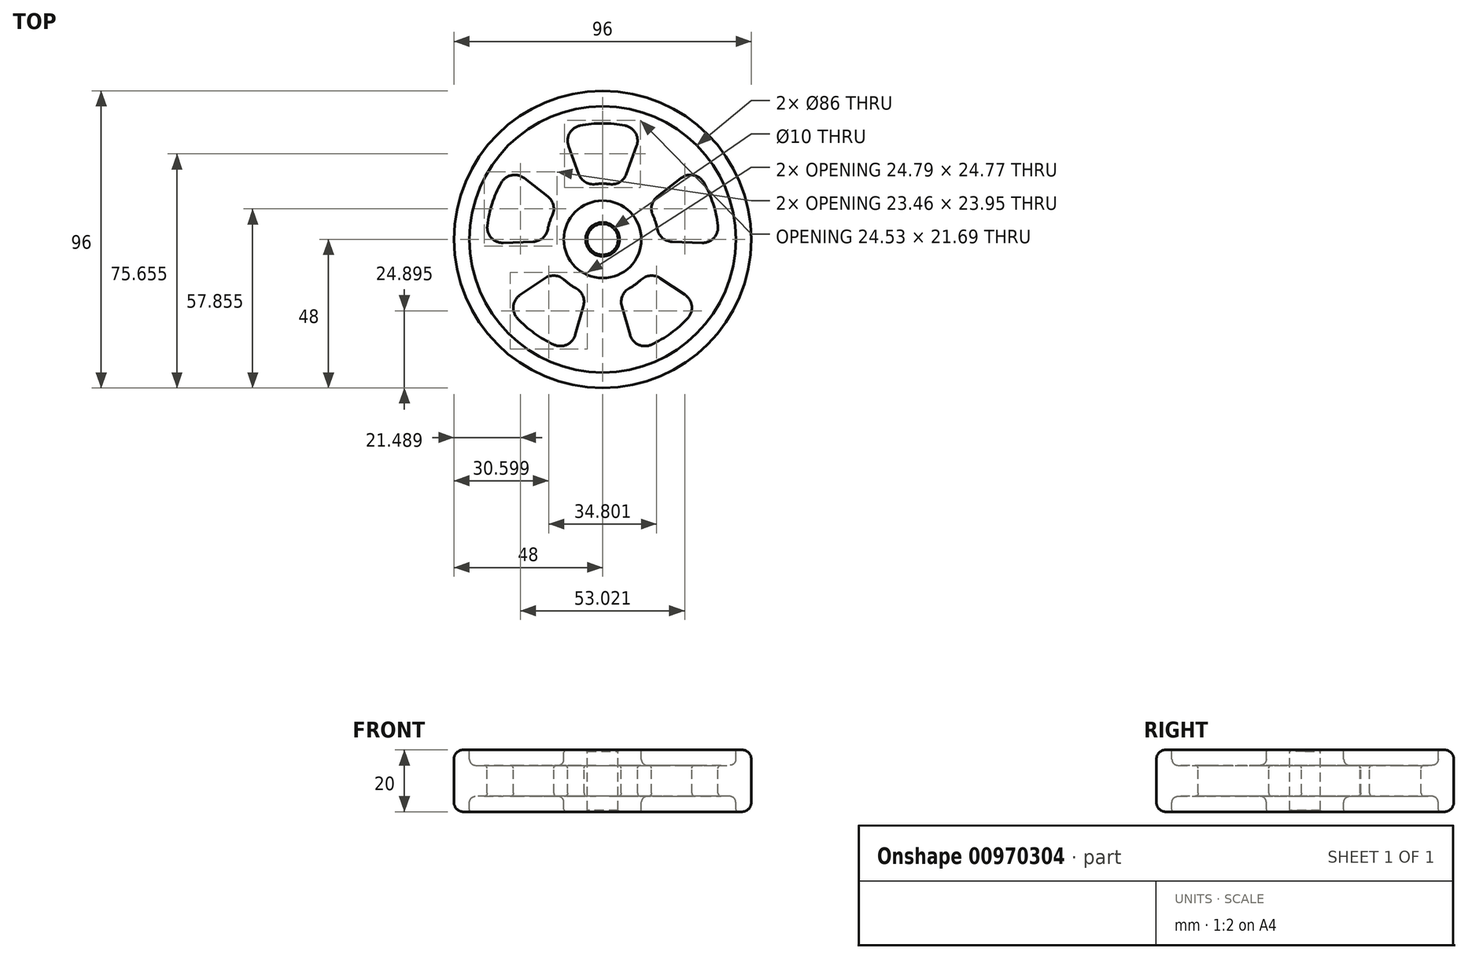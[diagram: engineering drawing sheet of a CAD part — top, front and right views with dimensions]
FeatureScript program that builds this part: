
annotation { "Feature Type Name" : "Feature", "Feature Type Description" : "" }
export const myFeature = defineFeature(function(context is Context, id is Id, definition is map)
    precondition{}
    {
        {
            var Q0;
            Q0=qCreatedBy(makeId("Front.planeOp"),FACE);
            var sketch = newSketch(context, id + "F0", { "sketchPlane" : qUnion([Q0])});
            skLineSegment(sketch, "E0", {"start": v(-5, 0) * mm, "end": v(-5, -20) * mm});
            skLineSegment(sketch, "E1", {"start": v(-5, -20) * mm, "end": v(-12.5, -20) * mm});
            skLineSegment(sketch, "E2", {"start": v(-12.5, -20) * mm, "end": v(-12.5, -15) * mm});
            skLineSegment(sketch, "E3", {"start": v(-12.5, -15) * mm, "end": v(-43, -15) * mm});
            skLineSegment(sketch, "E4", {"start": v(-43, -15) * mm, "end": v(-43, -20) * mm});
            skLineSegment(sketch, "E5", {"start": v(-43, -20) * mm, "end": v(-48, -20) * mm});
            skLineSegment(sketch, "E6", {"start": v(-48, -20) * mm, "end": v(-48, 0) * mm});
            skLineSegment(sketch, "E7", {"start": v(-48, 0) * mm, "end": v(-43, 0) * mm});
            skLineSegment(sketch, "E8", {"start": v(-43, 0) * mm, "end": v(-43, -5) * mm});
            skLineSegment(sketch, "E9", {"start": v(-43, -5) * mm, "end": v(-12.5, -5) * mm});
            skLineSegment(sketch, "E10", {"start": v(-12.5, -5) * mm, "end": v(-12.5, 0) * mm});
            skLineSegment(sketch, "E11", {"start": v(-12.5, 0) * mm, "end": v(-5, 0) * mm});
            skPoint(sketch, "E12.end.orphan", {"position": v(-12.5, -2.5) * mm});
            skLineSegment(sketch, "E13", {"start": v(0, 0) * mm, "end": v(0, -17.94) * mm});
            skSolve(sketch);
        }
        {
            var Q0;
            Q0=makeQuery(id+"F0.imprint","IMPRINT",FACE,{"disambiguationData":[TD([[makeQuery(id+"F0.imprint","IMPRINT",EDGE,{"derivedFrom":sQuery(id+"F0.wireOp",EDGE,"E0")}),-1.0]])]});
            var Q1;
            Q1=sQuery(id+"F0.wireOp",EDGE,"E13");
            revolve(context, id + "F1", {"surfaceOperationType" : NewSurfaceOperationType.NEW, "entities" : qUnion([Q0]), "axis" : qUnion([Q1]), "revolveType" : RevolveType.FULL});
        }
        {
            var Q0;
            Q0=makeQuery(id+"F1.opRevolve","SWEPT_EDGE",EDGE,{"disambiguationData":[OSD([sQuery(id+"F0.wireOp",EDGE,"E9"),sQuery(id+"F0.wireOp",EDGE,"E10")])]});
            var Q1;
            Q1=makeQuery(id+"F1.opRevolve","SWEPT_EDGE",EDGE,{"disambiguationData":[OSD([sQuery(id+"F0.wireOp",EDGE,"E8"),sQuery(id+"F0.wireOp",EDGE,"E9")])]});
            var Q2;
            Q2=makeQuery(id+"F1.opRevolve","SWEPT_EDGE",EDGE,{"disambiguationData":[OSD([sQuery(id+"F0.wireOp",EDGE,"E2"),sQuery(id+"F0.wireOp",EDGE,"E3")])]});
            var Q3;
            Q3=makeQuery(id+"F1.opRevolve","SWEPT_EDGE",EDGE,{"disambiguationData":[OSD([sQuery(id+"F0.wireOp",EDGE,"E3"),sQuery(id+"F0.wireOp",EDGE,"E4")])]});
            fillet(context, id + "F2", {"entities" : qUnion([Q0, Q1, Q2, Q3]), "radius" : 2 * mm, "tangentPropagation" : true, "allowEdgeOverflow" : false});
        }
        {
            var Q0;
            Q0=makeQuery(id+"F1.opRevolve","SWEPT_EDGE",EDGE,{"disambiguationData":[OSD([sQuery(id+"F0.wireOp",EDGE,"E6"),sQuery(id+"F0.wireOp",EDGE,"E7")])]});
            var Q1;
            Q1=makeQuery(id+"F1.opRevolve","SWEPT_EDGE",EDGE,{"disambiguationData":[OSD([sQuery(id+"F0.wireOp",EDGE,"E5"),sQuery(id+"F0.wireOp",EDGE,"E6")])]});
            fillet(context, id + "F3", {"entities" : qUnion([Q0, Q1]), "radius" : 3 * mm, "tangentPropagation" : true, "allowEdgeOverflow" : false});
        }
        {
            var Q0;
            Q0=makeQuery(id+"F1.opRevolve","SWEPT_FACE",FACE,{"disambiguationData":[OSD([sQuery(id+"F0.wireOp",EDGE,"E4")])]});
            var Q1;
            Q1=makeQuery(id+"F1.opRevolve","SWEPT_FACE",FACE,{"disambiguationData":[OSD([sQuery(id+"F0.wireOp",EDGE,"E8")])]});
            var Q2;
            Q2=makeQuery(id+"F1.opRevolve","SWEPT_EDGE",EDGE,{"disambiguationData":[OSD([sQuery(id+"F0.wireOp",EDGE,"E1"),sQuery(id+"F0.wireOp",EDGE,"E2")])]});
            var Q3;
            Q3=makeQuery(id+"F1.opRevolve","SWEPT_EDGE",EDGE,{"disambiguationData":[OSD([sQuery(id+"F0.wireOp",EDGE,"E10"),sQuery(id+"F0.wireOp",EDGE,"E11")])]});
            fillet(context, id + "F4", {"entities" : qUnion([Q0, Q1, Q2, Q3]), "radius" : .75 * mm, "tangentPropagation" : true, "allowEdgeOverflow" : false});
        }
        {
            var Q0;
            Q0=qCreatedBy(makeId("Top.planeOp"),FACE);
            var sketch = newSketch(context, id + "F5", { "sketchPlane" : qUnion([Q0])});
            skArc(sketch, "E14", {"start": v(6.16, 16.91) * mm, "mid": v(0, 18) * mm, "end": v(-6.16, 16.91) * mm});
            skArc(sketch, "E15", {"start": v(12.83, 35.24) * mm, "mid": v(0, 37.5) * mm, "end": v(-12.83, 35.24) * mm});
            skLineSegment(sketch, "E16", {"start": v(-6.16, 16.91) * mm, "end": v(-12.83, 35.24) * mm});
            skLineSegment(sketch, "E17", {"start": v(6.16, 16.91) * mm, "end": v(12.85, 35.32) * mm});
            skArc(sketch, "E18.1.0", {"start": v(-29.55, 23.09) * mm, "mid": v(-35.66, 11.59) * mm, "end": v(-37.48, -1.3) * mm});
            skLineSegment(sketch, "E18.1.1", {"start": v(-17.99, -0.63) * mm, "end": v(-37.48, -1.3) * mm});
            skArc(sketch, "E18.1.2", {"start": v(-14.18, 11.08) * mm, "mid": v(-17.12, 5.56) * mm, "end": v(-17.99, -0.63) * mm});
            skLineSegment(sketch, "E18.1.3", {"start": v(-14.18, 11.08) * mm, "end": v(-29.62, 23.14) * mm});
            skArc(sketch, "E18.2.0", {"start": v(-31.09, -20.97) * mm, "mid": v(-22.04, -30.34) * mm, "end": v(-10.34, -36.05) * mm});
            skLineSegment(sketch, "E18.2.1", {"start": v(-4.96, -17.3) * mm, "end": v(-10.34, -36.05) * mm});
            skArc(sketch, "E18.2.2", {"start": v(-14.92, -10.07) * mm, "mid": v(-10.58, -14.56) * mm, "end": v(-4.96, -17.3) * mm});
            skLineSegment(sketch, "E18.2.3", {"start": v(-14.92, -10.07) * mm, "end": v(-31.16, -21.02) * mm});
            skArc(sketch, "E18.3.0", {"start": v(10.34, -36.05) * mm, "mid": v(22.04, -30.34) * mm, "end": v(31.09, -20.97) * mm});
            skLineSegment(sketch, "E18.3.1", {"start": v(14.92, -10.07) * mm, "end": v(31.09, -20.97) * mm});
            skArc(sketch, "E18.3.2", {"start": v(4.96, -17.3) * mm, "mid": v(10.58, -14.56) * mm, "end": v(14.92, -10.07) * mm});
            skLineSegment(sketch, "E18.3.3", {"start": v(4.96, -17.3) * mm, "end": v(10.36, -36.13) * mm});
            skArc(sketch, "E18.4.0", {"start": v(37.48, -1.3) * mm, "mid": v(35.66, 11.59) * mm, "end": v(29.55, 23.09) * mm});
            skLineSegment(sketch, "E18.4.1", {"start": v(14.18, 11.08) * mm, "end": v(29.55, 23.09) * mm});
            skArc(sketch, "E18.4.2", {"start": v(17.99, -0.63) * mm, "mid": v(17.12, 5.56) * mm, "end": v(14.18, 11.08) * mm});
            skLineSegment(sketch, "E18.4.3", {"start": v(17.99, -0.63) * mm, "end": v(37.56, -1.31) * mm});
            skSolve(sketch);
        }
        {
            var Q0;
            {var subQ0=sQuery(id+"F5.wireOp",EDGE,"E18.1.0");Q0=makeQuery(id+"F5.imprint","IMPRINT",FACE,{"disambiguationData":[TD([[makeQuery(id+"F5.imprint","IMPRINT",EDGE,{"derivedFrom":subQ0}),1.0]])]});}
            var Q1;
            {var subQ0=sQuery(id+"F5.wireOp",EDGE,"E14");Q1=makeQuery(id+"F5.imprint","IMPRINT",FACE,{"disambiguationData":[TD([[makeQuery(id+"F5.imprint","IMPRINT",EDGE,{"derivedFrom":subQ0}),-1.0]])]});}
            var Q2;
            {var subQ0=sQuery(id+"F5.wireOp",EDGE,"E18.4.0");Q2=makeQuery(id+"F5.imprint","IMPRINT",FACE,{"disambiguationData":[TD([[makeQuery(id+"F5.imprint","IMPRINT",EDGE,{"derivedFrom":subQ0}),1.0]])]});}
            var Q3;
            {var subQ0=sQuery(id+"F5.wireOp",EDGE,"E18.3.0");Q3=makeQuery(id+"F5.imprint","IMPRINT",FACE,{"disambiguationData":[TD([[makeQuery(id+"F5.imprint","IMPRINT",EDGE,{"derivedFrom":subQ0}),1.0]])]});}
            var Q4;
            {var subQ0=sQuery(id+"F5.wireOp",EDGE,"E18.2.0");Q4=makeQuery(id+"F5.imprint","IMPRINT",FACE,{"disambiguationData":[TD([[makeQuery(id+"F5.imprint","IMPRINT",EDGE,{"derivedFrom":subQ0}),1.0]])]});}
            extrude(context, id + "F6", {"entities" : qUnion([Q0, Q1, Q2, Q3, Q4]), "operationType" : NewBodyOperationType.REMOVE, "oppositeDirection" : true, "depth" : 25 * mm, "offsetDistance" : 25 * mm});
        }
        {
            var Q0;
            Q0=makeQuery(id+"F6.boolean.opBoolean","COPY",EDGE,{"derivedFrom":makeQuery(id+"F6.opExtrude","SWEPT_EDGE",EDGE,{"disambiguationData":[OSD([sQuery(id+"F5.wireOp",EDGE,"E18.1.0"),sQuery(id+"F5.wireOp",EDGE,"E18.1.3")])]})});
            var Q1;
            Q1=makeQuery(id+"F6.boolean.opBoolean","COPY",EDGE,{"derivedFrom":makeQuery(id+"F6.opExtrude","SWEPT_EDGE",EDGE,{"disambiguationData":[OSD([sQuery(id+"F5.wireOp",EDGE,"E18.4.0"),sQuery(id+"F5.wireOp",EDGE,"E18.4.1")])]})});
            var Q2;
            Q2=makeQuery(id+"F6.boolean.opBoolean","COPY",EDGE,{"derivedFrom":makeQuery(id+"F6.opExtrude","SWEPT_EDGE",EDGE,{"disambiguationData":[OSD([sQuery(id+"F5.wireOp",EDGE,"E18.2.2"),sQuery(id+"F5.wireOp",EDGE,"E18.2.3")])]})});
            var Q3;
            Q3=makeQuery(id+"F6.boolean.opBoolean","COPY",EDGE,{"derivedFrom":makeQuery(id+"F6.opExtrude","SWEPT_EDGE",EDGE,{"disambiguationData":[OSD([sQuery(id+"F5.wireOp",EDGE,"E18.3.1"),sQuery(id+"F5.wireOp",EDGE,"E18.3.2")])]})});
            var Q4;
            Q4=makeQuery(id+"F6.boolean.opBoolean","COPY",EDGE,{"derivedFrom":makeQuery(id+"F6.opExtrude","SWEPT_EDGE",EDGE,{"disambiguationData":[OSD([sQuery(id+"F5.wireOp",EDGE,"E18.3.2"),sQuery(id+"F5.wireOp",EDGE,"E18.3.3")])]})});
            var Q5;
            Q5=makeQuery(id+"F6.boolean.opBoolean","COPY",EDGE,{"derivedFrom":makeQuery(id+"F6.opExtrude","SWEPT_EDGE",EDGE,{"disambiguationData":[OSD([sQuery(id+"F5.wireOp",EDGE,"E18.2.0"),sQuery(id+"F5.wireOp",EDGE,"E18.2.3")])]})});
            var Q6;
            Q6=makeQuery(id+"F6.boolean.opBoolean","COPY",EDGE,{"derivedFrom":makeQuery(id+"F6.opExtrude","SWEPT_EDGE",EDGE,{"disambiguationData":[OSD([sQuery(id+"F5.wireOp",EDGE,"E15"),sQuery(id+"F5.wireOp",EDGE,"E16")])]})});
            var Q7;
            Q7=makeQuery(id+"F6.boolean.opBoolean","COPY",EDGE,{"derivedFrom":makeQuery(id+"F6.opExtrude","SWEPT_EDGE",EDGE,{"disambiguationData":[OSD([sQuery(id+"F5.wireOp",EDGE,"E15"),sQuery(id+"F5.wireOp",EDGE,"E17")])]})});
            var Q8;
            Q8=makeQuery(id+"F6.boolean.opBoolean","COPY",EDGE,{"derivedFrom":makeQuery(id+"F6.opExtrude","SWEPT_EDGE",EDGE,{"disambiguationData":[OSD([sQuery(id+"F5.wireOp",EDGE,"E18.3.0"),sQuery(id+"F5.wireOp",EDGE,"E18.3.1")])]})});
            var Q9;
            Q9=makeQuery(id+"F6.boolean.opBoolean","COPY",EDGE,{"derivedFrom":makeQuery(id+"F6.opExtrude","SWEPT_EDGE",EDGE,{"disambiguationData":[OSD([sQuery(id+"F5.wireOp",EDGE,"E18.2.0"),sQuery(id+"F5.wireOp",EDGE,"E18.2.1")])]})});
            var Q10;
            Q10=makeQuery(id+"F6.boolean.opBoolean","COPY",EDGE,{"derivedFrom":makeQuery(id+"F6.opExtrude","SWEPT_EDGE",EDGE,{"disambiguationData":[OSD([sQuery(id+"F5.wireOp",EDGE,"E18.4.0"),sQuery(id+"F5.wireOp",EDGE,"E18.4.3")])]})});
            var Q11;
            Q11=makeQuery(id+"F6.boolean.opBoolean","COPY",EDGE,{"derivedFrom":makeQuery(id+"F6.opExtrude","SWEPT_EDGE",EDGE,{"disambiguationData":[OSD([sQuery(id+"F5.wireOp",EDGE,"E18.3.0"),sQuery(id+"F5.wireOp",EDGE,"E18.3.3")])]})});
            var Q12;
            Q12=makeQuery(id+"F6.boolean.opBoolean","COPY",EDGE,{"derivedFrom":makeQuery(id+"F6.opExtrude","SWEPT_EDGE",EDGE,{"disambiguationData":[OSD([sQuery(id+"F5.wireOp",EDGE,"E18.1.0"),sQuery(id+"F5.wireOp",EDGE,"E18.1.1")])]})});
            var Q13;
            Q13=makeQuery(id+"F6.boolean.opBoolean","COPY",EDGE,{"derivedFrom":makeQuery(id+"F6.opExtrude","SWEPT_EDGE",EDGE,{"disambiguationData":[OSD([sQuery(id+"F5.wireOp",EDGE,"E18.4.2"),sQuery(id+"F5.wireOp",EDGE,"E18.4.3")])]})});
            var Q14;
            Q14=makeQuery(id+"F6.boolean.opBoolean","COPY",EDGE,{"derivedFrom":makeQuery(id+"F6.opExtrude","SWEPT_EDGE",EDGE,{"disambiguationData":[OSD([sQuery(id+"F5.wireOp",EDGE,"E14"),sQuery(id+"F5.wireOp",EDGE,"E16")])]})});
            var Q15;
            Q15=makeQuery(id+"F6.boolean.opBoolean","COPY",EDGE,{"derivedFrom":makeQuery(id+"F6.opExtrude","SWEPT_EDGE",EDGE,{"disambiguationData":[OSD([sQuery(id+"F5.wireOp",EDGE,"E18.2.1"),sQuery(id+"F5.wireOp",EDGE,"E18.2.2")])]})});
            var Q16;
            Q16=makeQuery(id+"F6.boolean.opBoolean","COPY",EDGE,{"derivedFrom":makeQuery(id+"F6.opExtrude","SWEPT_EDGE",EDGE,{"disambiguationData":[OSD([sQuery(id+"F5.wireOp",EDGE,"E18.1.2"),sQuery(id+"F5.wireOp",EDGE,"E18.1.3")])]})});
            var Q17;
            Q17=makeQuery(id+"F6.boolean.opBoolean","COPY",EDGE,{"derivedFrom":makeQuery(id+"F6.opExtrude","SWEPT_EDGE",EDGE,{"disambiguationData":[OSD([sQuery(id+"F5.wireOp",EDGE,"E18.4.1"),sQuery(id+"F5.wireOp",EDGE,"E18.4.2")])]})});
            var Q18;
            Q18=makeQuery(id+"F6.boolean.opBoolean","COPY",EDGE,{"derivedFrom":makeQuery(id+"F6.opExtrude","SWEPT_EDGE",EDGE,{"disambiguationData":[OSD([sQuery(id+"F5.wireOp",EDGE,"E14"),sQuery(id+"F5.wireOp",EDGE,"E17")])]})});
            var Q19;
            Q19=makeQuery(id+"F6.boolean.opBoolean","COPY",EDGE,{"derivedFrom":makeQuery(id+"F6.opExtrude","SWEPT_EDGE",EDGE,{"disambiguationData":[OSD([sQuery(id+"F5.wireOp",EDGE,"E18.1.1"),sQuery(id+"F5.wireOp",EDGE,"E18.1.2")])]})});
            fillet(context, id + "F7", {"entities" : qUnion([Q0, Q1, Q2, Q3, Q4, Q5, Q6, Q7, Q8, Q9, Q10, Q11, Q12, Q13, Q14, Q15, Q16, Q17, Q18, Q19]), "radius" : 5 * mm, "tangentPropagation" : true, "allowEdgeOverflow" : false});
        }
        {
            var Q0;
            Q0=makeQuery(id+"F6.boolean.opBoolean","INTERSECT",EDGE,{"derivedFrom":[makeQuery(id+"F1.opRevolve","SWEPT_FACE",FACE,{"disambiguationData":[OSD([sQuery(id+"F0.wireOp",EDGE,"E9")])]}),makeQuery(id+"F6.opExtrude","SWEPT_FACE",FACE,{"disambiguationData":[OSD([sQuery(id+"F5.wireOp",EDGE,"E18.1.3")])]})]});
            var Q1;
            Q1=makeQuery(id+"F7.opFillet","BLEND_EDGE",EDGE,{"blendedFrom":[makeQuery(id+"F6.boolean.opBoolean","COPY",EDGE,{"derivedFrom":makeQuery(id+"F6.opExtrude","SWEPT_EDGE",EDGE,{"disambiguationData":[OSD([sQuery(id+"F5.wireOp",EDGE,"E15"),sQuery(id+"F5.wireOp",EDGE,"E17")])]})}),makeQuery(id+"F1.opRevolve","SWEPT_FACE",FACE,{"disambiguationData":[OSD([sQuery(id+"F0.wireOp",EDGE,"E9")])]})],"blendedInto":[makeQuery(id+"F1.opRevolve","SWEPT_FACE",FACE,{"disambiguationData":[OSD([sQuery(id+"F0.wireOp",EDGE,"E9")])]})]});
            var Q2;
            Q2=makeQuery(id+"F6.boolean.opBoolean","INTERSECT",EDGE,{"derivedFrom":[makeQuery(id+"F1.opRevolve","SWEPT_FACE",FACE,{"disambiguationData":[OSD([sQuery(id+"F0.wireOp",EDGE,"E9")])]}),makeQuery(id+"F6.opExtrude","SWEPT_FACE",FACE,{"disambiguationData":[OSD([sQuery(id+"F5.wireOp",EDGE,"E18.4.0")])]})]});
            var Q3;
            Q3=makeQuery(id+"F6.boolean.opBoolean","INTERSECT",EDGE,{"derivedFrom":[makeQuery(id+"F1.opRevolve","SWEPT_FACE",FACE,{"disambiguationData":[OSD([sQuery(id+"F0.wireOp",EDGE,"E9")])]}),makeQuery(id+"F6.opExtrude","SWEPT_FACE",FACE,{"disambiguationData":[OSD([sQuery(id+"F5.wireOp",EDGE,"E18.3.1")])]})]});
            var Q4;
            Q4=makeQuery(id+"F6.boolean.opBoolean","INTERSECT",EDGE,{"derivedFrom":[makeQuery(id+"F1.opRevolve","SWEPT_FACE",FACE,{"disambiguationData":[OSD([sQuery(id+"F0.wireOp",EDGE,"E9")])]}),makeQuery(id+"F6.opExtrude","SWEPT_FACE",FACE,{"disambiguationData":[OSD([sQuery(id+"F5.wireOp",EDGE,"E18.2.3")])]})]});
            var Q5;
            Q5=makeQuery(id+"F6.boolean.opBoolean","INTERSECT",EDGE,{"derivedFrom":[makeQuery(id+"F1.opRevolve","SWEPT_FACE",FACE,{"disambiguationData":[OSD([sQuery(id+"F0.wireOp",EDGE,"E3")])]}),makeQuery(id+"F6.opExtrude","SWEPT_FACE",FACE,{"disambiguationData":[OSD([sQuery(id+"F5.wireOp",EDGE,"E18.3.0")])]})]});
            var Q6;
            Q6=makeQuery(id+"F6.boolean.opBoolean","INTERSECT",EDGE,{"derivedFrom":[makeQuery(id+"F1.opRevolve","SWEPT_FACE",FACE,{"disambiguationData":[OSD([sQuery(id+"F0.wireOp",EDGE,"E3")])]}),makeQuery(id+"F6.opExtrude","SWEPT_FACE",FACE,{"disambiguationData":[OSD([sQuery(id+"F5.wireOp",EDGE,"E18.4.0")])]})]});
            var Q7;
            Q7=makeQuery(id+"F6.boolean.opBoolean","INTERSECT",EDGE,{"derivedFrom":[makeQuery(id+"F1.opRevolve","SWEPT_FACE",FACE,{"disambiguationData":[OSD([sQuery(id+"F0.wireOp",EDGE,"E3")])]}),makeQuery(id+"F6.opExtrude","SWEPT_FACE",FACE,{"disambiguationData":[OSD([sQuery(id+"F5.wireOp",EDGE,"E18.2.1")])]})]});
            var Q8;
            Q8=makeQuery(id+"F6.boolean.opBoolean","INTERSECT",EDGE,{"derivedFrom":[makeQuery(id+"F1.opRevolve","SWEPT_FACE",FACE,{"disambiguationData":[OSD([sQuery(id+"F0.wireOp",EDGE,"E3")])]}),makeQuery(id+"F6.opExtrude","SWEPT_FACE",FACE,{"disambiguationData":[OSD([sQuery(id+"F5.wireOp",EDGE,"E18.1.1")])]})]});
            var Q9;
            Q9=makeQuery(id+"F6.boolean.opBoolean","INTERSECT",EDGE,{"derivedFrom":[makeQuery(id+"F1.opRevolve","SWEPT_FACE",FACE,{"disambiguationData":[OSD([sQuery(id+"F0.wireOp",EDGE,"E3")])]}),makeQuery(id+"F6.opExtrude","SWEPT_FACE",FACE,{"disambiguationData":[OSD([sQuery(id+"F5.wireOp",EDGE,"E17")])]})]});
            fillet(context, id + "F8", {"entities" : qUnion([Q0, Q1, Q2, Q3, Q4, Q5, Q6, Q7, Q8, Q9]), "radius" : 1 * mm, "tangentPropagation" : true, "allowEdgeOverflow" : false});
        }
        {
            var Q0;
            Q0=makeQuery(id+"F1.opRevolve","SWEPT_FACE",FACE,{"disambiguationData":[OSD([sQuery(id+"F0.wireOp",EDGE,"E1")])]});
            var Q1;
            Q1=makeQuery(id+"F1.opRevolve","SWEPT_FACE",FACE,{"disambiguationData":[OSD([sQuery(id+"F0.wireOp",EDGE,"E0")])]});
            chamfer(context, id + "F9", {"entities" : qUnion([Q0, Q1]), "width" : .5 * mm, "tangentPropagation" : true});
        }
    });
